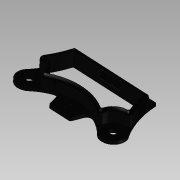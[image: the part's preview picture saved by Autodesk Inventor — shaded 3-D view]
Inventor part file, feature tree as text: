
AUTODESK INVENTOR PART (.ipt)
format: ipt  version: 2015 SP1 (Build 190203100, 203)  size: 631,808 bytes
history: native  units: mm
features: extrude x16, sketch x16, fillet x10, projected_geometry x7, plane x2
ambient origin geometry x8: Origin, YZ Plane, XZ Plane, XY Plane, X Axis, Y Axis, Z Axis, Center Point
bodies: Solid1 (feature_tree)
feature tree (51):
  extrude  "Extrusion1"  Depth=3.5mm
  extrude  "Extrusion2"  Depth=3.5mm TaperAngle=0.0deg
  extrude  "Extrusion3"  Depth=3.5mm TaperAngle=0.0deg
  extrude  "Extrusion4"  Depth=13.5mm TaperAngle=0.0deg
  extrude  "Extrusion5"  Depth=13.5mm TaperAngle=0.0deg
  extrude  "Extrusion6"  Depth=13.5mm TaperAngle=0.0deg
  extrude  "Extrusion8"  Depth=3.5mm TaperAngle=0.0deg
  extrude  "Extrusion9"  Depth=4.4125mm
  extrude  "Extrusion10"  TaperAngle=45.0deg  [1 undecoded]
  plane  "Work Plane1"
  extrude  "Extrusion11"  Depth=3.5mm
  fillet  "Fillet4"  Radius=3.5mm
  fillet  "Fillet5"  Radius=1.0mm
  fillet  "Fillet6"  Radius=1.0mm
  fillet  "Fillet7"  Radius=1.0mm
  fillet  "Fillet8"  Radius=3.5mm
  fillet  "Fillet9"  Radius=1.0mm
  fillet  "Fillet10"  Radius=10.0mm
  extrude  "Extrusion14"  Depth=12.5mm
  extrude  "Extrusion15"  Depth=5.0mm
  fillet  "Fillet11"  [1 undecoded]
  fillet  "Fillet12"  Radius=25.0mm
  extrude  "Extrusion16"  Depth=2.5mm
  plane  "Work Plane3"
  extrude  "Extrusion17"  Depth=1.0mm
  extrude  "Extrusion18"  Depth=7.0mm
  extrude  "Extrusion19"  Depth=0.95mm TaperAngle=0.0deg
  fillet  "Fillet13"  [1 undecoded]
  sketch  "Sketch1"  dims[d13=3.5mm d16=3.5mm]
  sketch  "Sketch2"  dims[d24=90.0deg d25=3.5mm d26=0.0mm]
  sketch  "Sketch3"  dims[d30=8.907301mm d32=3.5mm d33=0.0mm]
  projected_geometry  "Projected Loop1"
  sketch  "Sketch4"  dims[d34=13.5mm d35=0.0mm d38=13.5mm d39=0.0mm]
  sketch  "Sketch5"  dims[d40=31.55mm d41=13.5mm d42=0.0mm]
  projected_geometry  "Projected Loop2"
  sketch  "Sketch7"  dims[d44=3.5mm d45=0.0mm d51=13.5mm d52=0.0mm]
  projected_geometry  "Projected Loop3"
  sketch  "Sketch13"  dims[d53=3.5mm d54=0.0mm d55=3.5mm d56=0.0mm]
  projected_geometry  "Projected Loop5"
  sketch  "Sketch14"  dims[d57=0.0mm d58=4.4125mm]
  projected_geometry  "Projected Loop6"
  sketch  "Sketch15"  dims[d59=90.0deg d60=45.0deg]
  projected_geometry  "Projected Loop7"
  sketch  "Sketch16"  dims[d61=50.0mm d62=0.0mm d67=3.5mm d68=3.5mm d69=1.0mm d70=1.0mm d75=1.0mm d103=3.5mm d104=1.0mm d108=10.0mm d109=0.0mm]
  sketch  "Sketch27"  dims[d110=180.0deg d111=12.5mm]
  sketch  "Sketch28"  dims[d113=25.0mm d115=5.0mm d116=90.0deg d117=25.0mm]
  projected_geometry  "Projected Loop11"
  sketch  "Sketch29"  dims[d118=90.0deg d119=2.5mm]
  sketch  "Sketch32"  dims[d120=30.0mm d121=0.0mm d122=1.0mm]
  sketch  "Sketch33"  dims[d123=1.0mm d124=7.0mm]
  sketch  "Sketch34"  dims[d125=7.0mm d126=3.5mm d127=0.0mm d151=0.0mm d172=3.5mm d173=0.0mm d174=3.5mm d175=0.0mm d176=46.987913mm d177=12.022738mm d178=3.5mm d179=3.5mm d180=0.0mm d181=0.95mm]
note: 3 required parameter values undecoded (feature->parameter linkage not recoverable at this tier; creation-order binding heuristic only, values carry confidence <= 0.55)
